# Revit family: Сливная заглушка SX 10622
name_source: partatom
category: Арматура трубопроводов
revit_build: Autodesk Revit 2017 (Build: 20171027_0315(x64)
units: mm (PartAtom-declared; Revit-internal decimal feet)

## family parameters
Всегда вертикально = Да
На основе рабочей плоскости = Нет
Общий = Нет
При загрузке вырезать с полостями = Нет
Размер круглого соединителя = Использовать радиус
Тип детали = Вставляется

## types (2) — shared parameters
ADSK_Единица измерения = шт
ADSK_Завод-изготовитель = Meibes
ADSK_Наименование = Заглушка сливная Simplex, тип I
B = 13 мм
B/2-1 = 6 мм
URL = http://www.meibes.ru
Изготовитель = Meibes
Ключевая пометка = Заглушка сливная Simplex, тип I
Материал полимера = Фильтр_Черный
Материал стальной части = Сталь
Материал фитинга = РВК_Полипропилен PPR
Разработчик = ООО ПРОРУБИМ
Разработчик (телефон) = +7(495)649-85-43
Разработчик модели (URL) = http://prorubim.com
zero-valued in all types: ADSK_Масса

## per-type parameters (varying)
| type | ADSK_Код изделия | C | C1 | D | DN | R | s | x |
| DN15 | F10622 | 30 мм | 12 мм | 8 мм | 15 мм | 8 мм | 20 мм | 18 мм |
| DN10 | F10623 | 24 мм | 9 мм | 7 мм | 10 мм | 5 мм | 15 мм | 14 мм |

note: column(s) folded — value = type name in every type: ADSK_Обозначение
